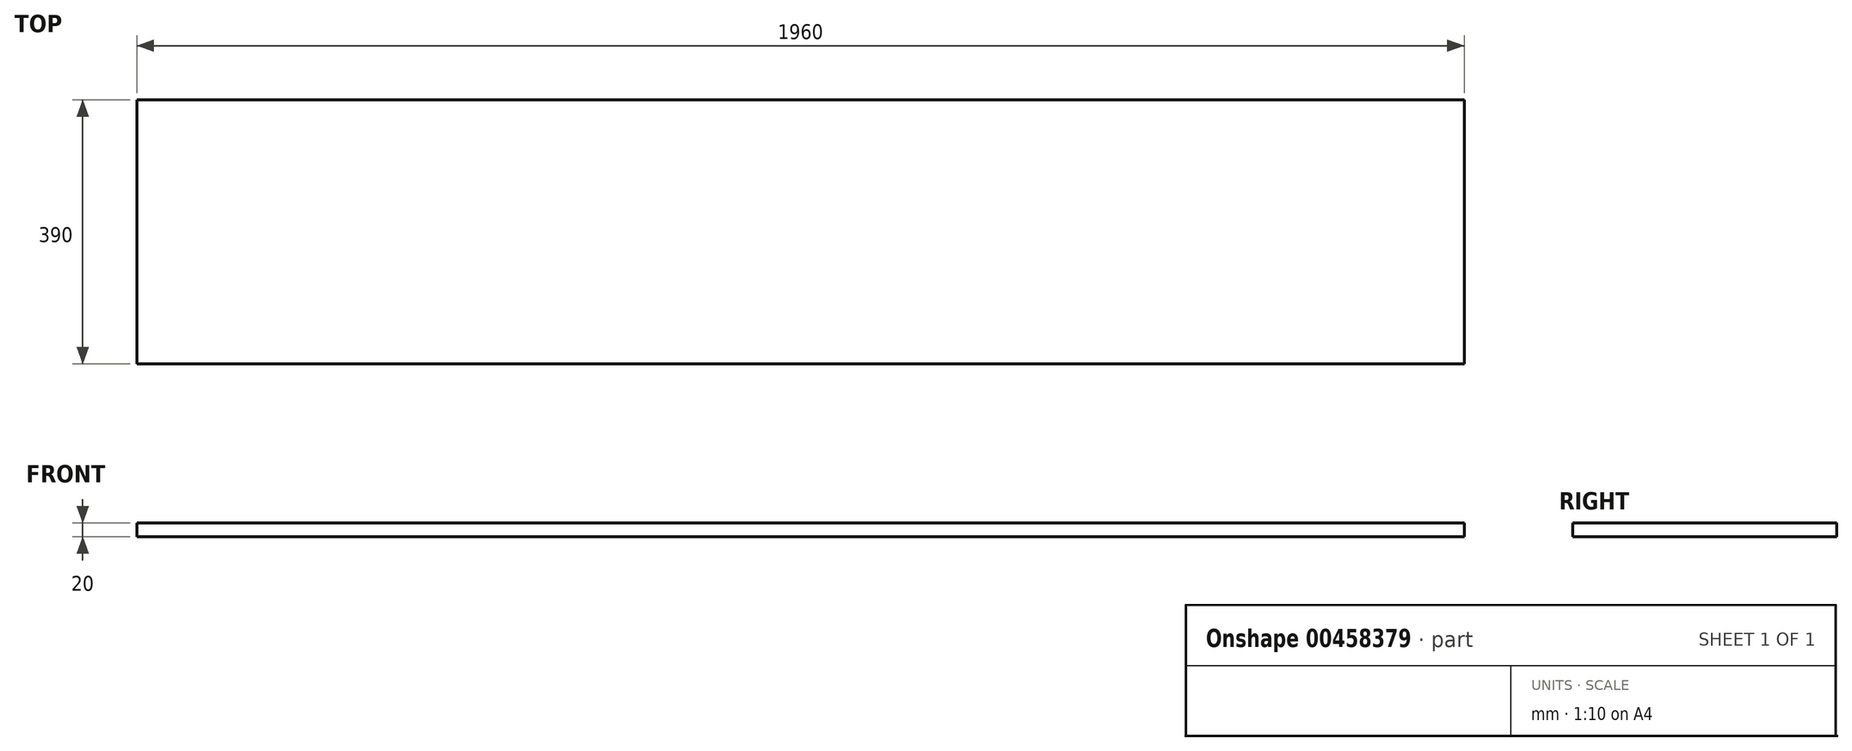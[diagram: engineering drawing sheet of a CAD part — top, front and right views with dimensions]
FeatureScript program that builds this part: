
annotation { "Feature Type Name" : "Feature", "Feature Type Description" : "" }
export const myFeature = defineFeature(function(context is Context, id is Id, definition is map)
    precondition{}
    {
        {
            var Q0;
            Q0=qCreatedBy(makeId("Top.planeOp"),FACE);
            var sketch = newSketch(context, id + "F0", { "sketchPlane" : qUnion([Q0])});
            skLineSegment(sketch, "E0.bottom", {"start": v(-1920.88, 378.5) * mm, "end": v(39.12, 378.5) * mm});
            skLineSegment(sketch, "E0.top", {"start": v(-1920.88, -11.5) * mm, "end": v(39.12, -11.5) * mm});
            skLineSegment(sketch, "E0.left", {"start": v(-1920.88, 378.5) * mm, "end": v(-1920.88, -11.5) * mm});
            skLineSegment(sketch, "E0.right", {"start": v(39.12, 378.5) * mm, "end": v(39.12, -11.5) * mm});
            skSolve(sketch);
        }
        {
            var Q0;
            Q0 = qSketchRegion(id + "F0", true);
            extrude(context, id + "F1", {"entities" : qUnion([Q0]), "depth" : 20 * mm});
        }
    });
